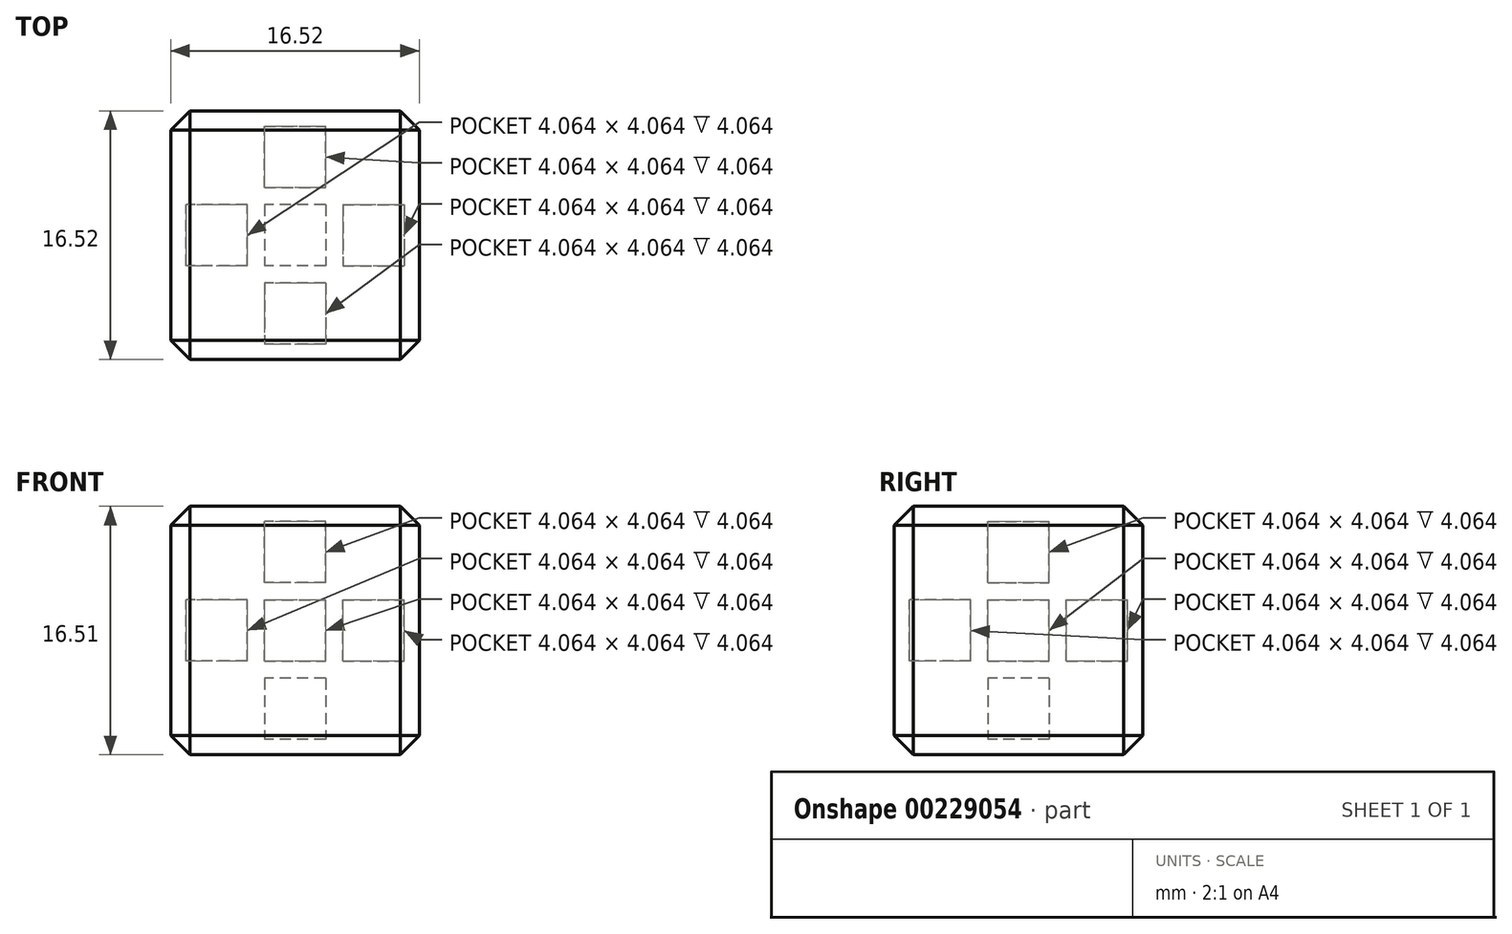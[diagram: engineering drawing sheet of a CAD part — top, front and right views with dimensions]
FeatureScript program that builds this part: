
annotation { "Feature Type Name" : "Feature", "Feature Type Description" : "" }
export const myFeature = defineFeature(function(context is Context, id is Id, definition is map)
    precondition{}
    {
        {
            var Q0;
            Q0=qCreatedBy(makeId("Top.planeOp"),FACE);
            var sketch = newSketch(context, id + "F0", { "sketchPlane" : qUnion([Q0])});
            skLineSegment(sketch, "E0.bottom", {"start": v(8.26, -8.26) * mm, "end": v(-8.26, -8.26) * mm});
            skLineSegment(sketch, "E0.top", {"start": v(8.26, 8.26) * mm, "end": v(-8.26, 8.26) * mm});
            skLineSegment(sketch, "E0.left", {"start": v(8.26, -8.26) * mm, "end": v(8.26, 8.26) * mm});
            skLineSegment(sketch, "E0.right", {"start": v(-8.26, -8.26) * mm, "end": v(-8.26, 8.26) * mm});
            skPoint(sketch, "E0.middle", {"position": v(0, 0) * mm});
            skSolve(sketch);
        }
        {
            var Q0;
            Q0 = qSketchRegion(id + "F0", true);
            extrude(context, id + "F1", {"entities" : qUnion([Q0]), "depth" : 16.5 * mm});
        }
        {
            var Q0;
            Q0=makeQuery(id+"F1.opExtrude","SWEPT_FACE",FACE,{"disambiguationData":[OSD([sQuery(id+"F0.wireOp",EDGE,"E0.right")])]});
            var Q1;
            Q1=makeQuery(id+"F1.opExtrude","SWEPT_EDGE",EDGE,{"disambiguationData":[OSD([sQuery(id+"F0.wireOp",EDGE,"E0.bottom"),sQuery(id+"F0.wireOp",EDGE,"E0.left")])]});
            var Q2;
            Q2=makeQuery(id+"F1.opExtrude","CAP_EDGE",EDGE,{"disambiguationData":[OSD([sQuery(id+"F0.wireOp",EDGE,"E0.bottom")])],"isStart":false});
            var Q3;
            Q3=makeQuery(id+"F1.opExtrude","SWEPT_FACE",FACE,{"disambiguationData":[OSD([sQuery(id+"F0.wireOp",EDGE,"E0.bottom")])]});
            var Q4;
            Q4=makeQuery(id+"F1.opExtrude","SWEPT_FACE",FACE,{"disambiguationData":[OSD([sQuery(id+"F0.wireOp",EDGE,"E0.top")])]});
            var Q5;
            Q5=makeQuery(id+"F1.opExtrude","SWEPT_FACE",FACE,{"disambiguationData":[OSD([sQuery(id+"F0.wireOp",EDGE,"E0.left")])]});
            chamfer(context, id + "F2", {"entities" : qUnion([Q0, Q1, Q2, Q3, Q4, Q5]), "width" : 1.27 * mm, "tangentPropagation" : true});
        }
        {
            var Q0;
            Q0=makeQuery(id+"F1.opExtrude","SWEPT_FACE",FACE,{"disambiguationData":[OSD([sQuery(id+"F0.wireOp",EDGE,"E0.bottom")])]});
            var sketch = newSketch(context, id + "F3", { "sketchPlane" : qUnion([Q0])});
            skLineSegment(sketch, "E1", {"start": v(0, 15.24) * mm, "end": v(0, 1.27) * mm, "construction": true});
            skLineSegment(sketch, "E2.bottom", {"start": v(2.03, 6.22) * mm, "end": v(-2.03, 6.22) * mm});
            skLineSegment(sketch, "E2.top", {"start": v(2.03, 10.29) * mm, "end": v(-2.03, 10.29) * mm});
            skLineSegment(sketch, "E2.left", {"start": v(2.03, 6.22) * mm, "end": v(2.03, 10.29) * mm});
            skLineSegment(sketch, "E2.right", {"start": v(-2.03, 6.22) * mm, "end": v(-2.03, 10.29) * mm});
            skPoint(sketch, "E2.middle", {"position": v(0, 8.26) * mm});
            skSolve(sketch);
        }
        {
            var Q0;
            Q0 = qSketchRegion(id + "F3", true);
            extrude(context, id + "F4", {"entities" : qUnion([Q0]), "operationType" : NewBodyOperationType.REMOVE, "oppositeDirection" : true, "depth" : 5.08 * mm});
        }
        {
            var Q0;
            Q0=makeQuery(id+"F1.opExtrude","SWEPT_FACE",FACE,{"disambiguationData":[OSD([sQuery(id+"F0.wireOp",EDGE,"E0.left")])]});
            var sketch = newSketch(context, id + "F5", { "sketchPlane" : qUnion([Q0])});
            skLineSegment(sketch, "E3", {"start": v(0, 15.24) * mm, "end": v(0, 1.27) * mm, "construction": true});
            skLineSegment(sketch, "E4.bottom", {"start": v(2.03, 6.22) * mm, "end": v(-2.03, 6.22) * mm});
            skLineSegment(sketch, "E4.top", {"start": v(2.03, 10.29) * mm, "end": v(-2.03, 10.29) * mm});
            skLineSegment(sketch, "E4.left", {"start": v(2.03, 6.22) * mm, "end": v(2.03, 10.29) * mm});
            skLineSegment(sketch, "E4.right", {"start": v(-2.03, 6.22) * mm, "end": v(-2.03, 10.29) * mm});
            skPoint(sketch, "E4.middle", {"position": v(0, 8.26) * mm});
            skSolve(sketch);
        }
        {
            var Q0;
            Q0 = qSketchRegion(id + "F5", true);
            extrude(context, id + "F6", {"entities" : qUnion([Q0]), "operationType" : NewBodyOperationType.REMOVE, "oppositeDirection" : true, "depth" : 5.08 * mm});
        }
        {
            var Q0;
            Q0=makeQuery(id+"F1.opExtrude","SWEPT_FACE",FACE,{"disambiguationData":[OSD([sQuery(id+"F0.wireOp",EDGE,"E0.top")])]});
            var sketch = newSketch(context, id + "F7", { "sketchPlane" : qUnion([Q0])});
            skLineSegment(sketch, "E5", {"start": v(0, 15.24) * mm, "end": v(0, 1.27) * mm, "construction": true});
            skLineSegment(sketch, "E6.bottom", {"start": v(2.03, 6.22) * mm, "end": v(-2.03, 6.22) * mm});
            skLineSegment(sketch, "E6.top", {"start": v(2.03, 10.29) * mm, "end": v(-2.03, 10.29) * mm});
            skLineSegment(sketch, "E6.left", {"start": v(2.03, 6.22) * mm, "end": v(2.03, 10.29) * mm});
            skLineSegment(sketch, "E6.right", {"start": v(-2.03, 6.22) * mm, "end": v(-2.03, 10.29) * mm});
            skPoint(sketch, "E6.middle", {"position": v(0, 8.26) * mm});
            skSolve(sketch);
        }
        {
            var Q0;
            Q0 = qSketchRegion(id + "F7", true);
            extrude(context, id + "F8", {"entities" : qUnion([Q0]), "operationType" : NewBodyOperationType.REMOVE, "oppositeDirection" : true, "depth" : 5.08 * mm});
        }
        {
            var Q0;
            Q0=makeQuery(id+"F1.opExtrude","SWEPT_FACE",FACE,{"disambiguationData":[OSD([sQuery(id+"F0.wireOp",EDGE,"E0.right")])]});
            var sketch = newSketch(context, id + "F9", { "sketchPlane" : qUnion([Q0])});
            skLineSegment(sketch, "E7", {"start": v(0, 15.24) * mm, "end": v(0, 1.27) * mm, "construction": true});
            skLineSegment(sketch, "E8.bottom", {"start": v(2.03, 6.22) * mm, "end": v(-2.03, 6.22) * mm});
            skLineSegment(sketch, "E8.top", {"start": v(2.03, 10.29) * mm, "end": v(-2.03, 10.29) * mm});
            skLineSegment(sketch, "E8.left", {"start": v(2.03, 6.22) * mm, "end": v(2.03, 10.29) * mm});
            skLineSegment(sketch, "E8.right", {"start": v(-2.03, 6.22) * mm, "end": v(-2.03, 10.29) * mm});
            skPoint(sketch, "E8.middle", {"position": v(0, 8.26) * mm});
            skSolve(sketch);
        }
        {
            var Q0;
            Q0 = qSketchRegion(id + "F9", true);
            extrude(context, id + "F10", {"entities" : qUnion([Q0]), "operationType" : NewBodyOperationType.REMOVE, "oppositeDirection" : true, "depth" : 5.08 * mm});
        }
        {
            var Q0;
            Q0=makeQuery(id+"F1.opExtrude","CAP_FACE",FACE,{"disambiguationData":[OSD([sQuery(id+"F0.wireOp",EDGE,"E0.bottom"),sQuery(id+"F0.wireOp",EDGE,"E0.top"),sQuery(id+"F0.wireOp",EDGE,"E0.left"),sQuery(id+"F0.wireOp",EDGE,"E0.right")])],"isStart":false});
            var sketch = newSketch(context, id + "F11", { "sketchPlane" : qUnion([Q0])});
            skLineSegment(sketch, "E9", {"start": v(0, 6.99) * mm, "end": v(0, -6.99) * mm, "construction": true});
            skLineSegment(sketch, "E10.bottom", {"start": v(2.03, -2.03) * mm, "end": v(-2.03, -2.03) * mm});
            skLineSegment(sketch, "E10.top", {"start": v(2.03, 2.03) * mm, "end": v(-2.03, 2.03) * mm});
            skLineSegment(sketch, "E10.left", {"start": v(2.03, -2.03) * mm, "end": v(2.03, 2.03) * mm});
            skLineSegment(sketch, "E10.right", {"start": v(-2.03, -2.03) * mm, "end": v(-2.03, 2.03) * mm});
            skPoint(sketch, "E10.middle", {"position": v(0, 0) * mm});
            skSolve(sketch);
        }
        {
            var Q0;
            Q0=makeQuery(id+"F11.imprint","IMPRINT",FACE,{"disambiguationData":[TD([[makeQuery(id+"F11.imprint","IMPRINT",EDGE,{"derivedFrom":sQuery(id+"F11.wireOp",EDGE,"E10.bottom")}),-1.0]])]});
            extrude(context, id + "F12", {"entities" : qUnion([Q0]), "operationType" : NewBodyOperationType.REMOVE, "oppositeDirection" : true, "depth" : 5.08 * mm});
        }
        {
            var Q0;
            Q0=makeQuery(id+"F1.opExtrude","CAP_FACE",FACE,{"disambiguationData":[OSD([sQuery(id+"F0.wireOp",EDGE,"E0.bottom"),sQuery(id+"F0.wireOp",EDGE,"E0.top"),sQuery(id+"F0.wireOp",EDGE,"E0.left"),sQuery(id+"F0.wireOp",EDGE,"E0.right")])],"isStart":true});
            var sketch = newSketch(context, id + "F13", { "sketchPlane" : qUnion([Q0])});
            skLineSegment(sketch, "E11", {"start": v(0, 6.99) * mm, "end": v(0, -6.99) * mm, "construction": true});
            skLineSegment(sketch, "E12.bottom", {"start": v(2.03, -2.03) * mm, "end": v(-2.03, -2.03) * mm});
            skLineSegment(sketch, "E12.top", {"start": v(2.03, 2.03) * mm, "end": v(-2.03, 2.03) * mm});
            skLineSegment(sketch, "E12.left", {"start": v(2.03, -2.03) * mm, "end": v(2.03, 2.03) * mm});
            skLineSegment(sketch, "E12.right", {"start": v(-2.03, -2.03) * mm, "end": v(-2.03, 2.03) * mm});
            skPoint(sketch, "E12.middle", {"position": v(0, 0) * mm});
            skSolve(sketch);
        }
        {
            var Q0;
            Q0=makeQuery(id+"F13.imprint","IMPRINT",FACE,{"disambiguationData":[TD([[makeQuery(id+"F13.imprint","IMPRINT",EDGE,{"derivedFrom":sQuery(id+"F13.wireOp",EDGE,"E12.bottom")}),-1.0]])]});
            extrude(context, id + "F14", {"entities" : qUnion([Q0]), "operationType" : NewBodyOperationType.REMOVE, "oppositeDirection" : true, "depth" : 5.08 * mm});
        }
        {
            var Q0;
            Q0=makeQuery(id+"F3.imprint","IMPRINT",FACE,{"disambiguationData":[TD([[makeQuery(id+"F3.imprint","IMPRINT",EDGE,{"derivedFrom":sQuery(id+"F3.wireOp",EDGE,"E2.bottom")}),-1.0]])]});
            extrude(context, id + "F15", {"entities" : qUnion([Q0]), "operationType" : NewBodyOperationType.ADD, "oppositeDirection" : true, "depth" : 1.02 * mm});
        }
        {
            var Q0;
            Q0=makeQuery(id+"F5.imprint","IMPRINT",FACE,{"disambiguationData":[TD([[makeQuery(id+"F5.imprint","IMPRINT",EDGE,{"derivedFrom":sQuery(id+"F5.wireOp",EDGE,"E4.bottom")}),-1.0]])]});
            extrude(context, id + "F16", {"entities" : qUnion([Q0]), "operationType" : NewBodyOperationType.ADD, "oppositeDirection" : true, "depth" : 1.02 * mm});
        }
        {
            var Q0;
            Q0=makeQuery(id+"F7.imprint","IMPRINT",FACE,{"disambiguationData":[TD([[makeQuery(id+"F7.imprint","IMPRINT",EDGE,{"derivedFrom":sQuery(id+"F7.wireOp",EDGE,"E6.bottom")}),-1.0]])]});
            extrude(context, id + "F17", {"entities" : qUnion([Q0]), "operationType" : NewBodyOperationType.ADD, "oppositeDirection" : true, "depth" : 1.02 * mm});
        }
        {
            var Q0;
            Q0=makeQuery(id+"F9.imprint","IMPRINT",FACE,{"disambiguationData":[TD([[makeQuery(id+"F9.imprint","IMPRINT",EDGE,{"derivedFrom":sQuery(id+"F9.wireOp",EDGE,"E8.bottom")}),-1.0]])]});
            extrude(context, id + "F18", {"entities" : qUnion([Q0]), "operationType" : NewBodyOperationType.ADD, "oppositeDirection" : true, "depth" : 1.02 * mm});
        }
        {
            var Q0;
            Q0=makeQuery(id+"F11.imprint","IMPRINT",FACE,{"disambiguationData":[TD([[makeQuery(id+"F11.imprint","IMPRINT",EDGE,{"derivedFrom":sQuery(id+"F11.wireOp",EDGE,"E10.bottom")}),-1.0]])]});
            extrude(context, id + "F19", {"entities" : qUnion([Q0]), "operationType" : NewBodyOperationType.ADD, "oppositeDirection" : true, "depth" : 1.02 * mm});
        }
        {
            var Q0;
            Q0=makeQuery(id+"F13.imprint","IMPRINT",FACE,{"disambiguationData":[TD([[makeQuery(id+"F13.imprint","IMPRINT",EDGE,{"derivedFrom":sQuery(id+"F13.wireOp",EDGE,"E12.bottom")}),-1.0]])]});
            extrude(context, id + "F20", {"entities" : qUnion([Q0]), "operationType" : NewBodyOperationType.ADD, "oppositeDirection" : true, "depth" : 1.02 * mm});
        }
    });
